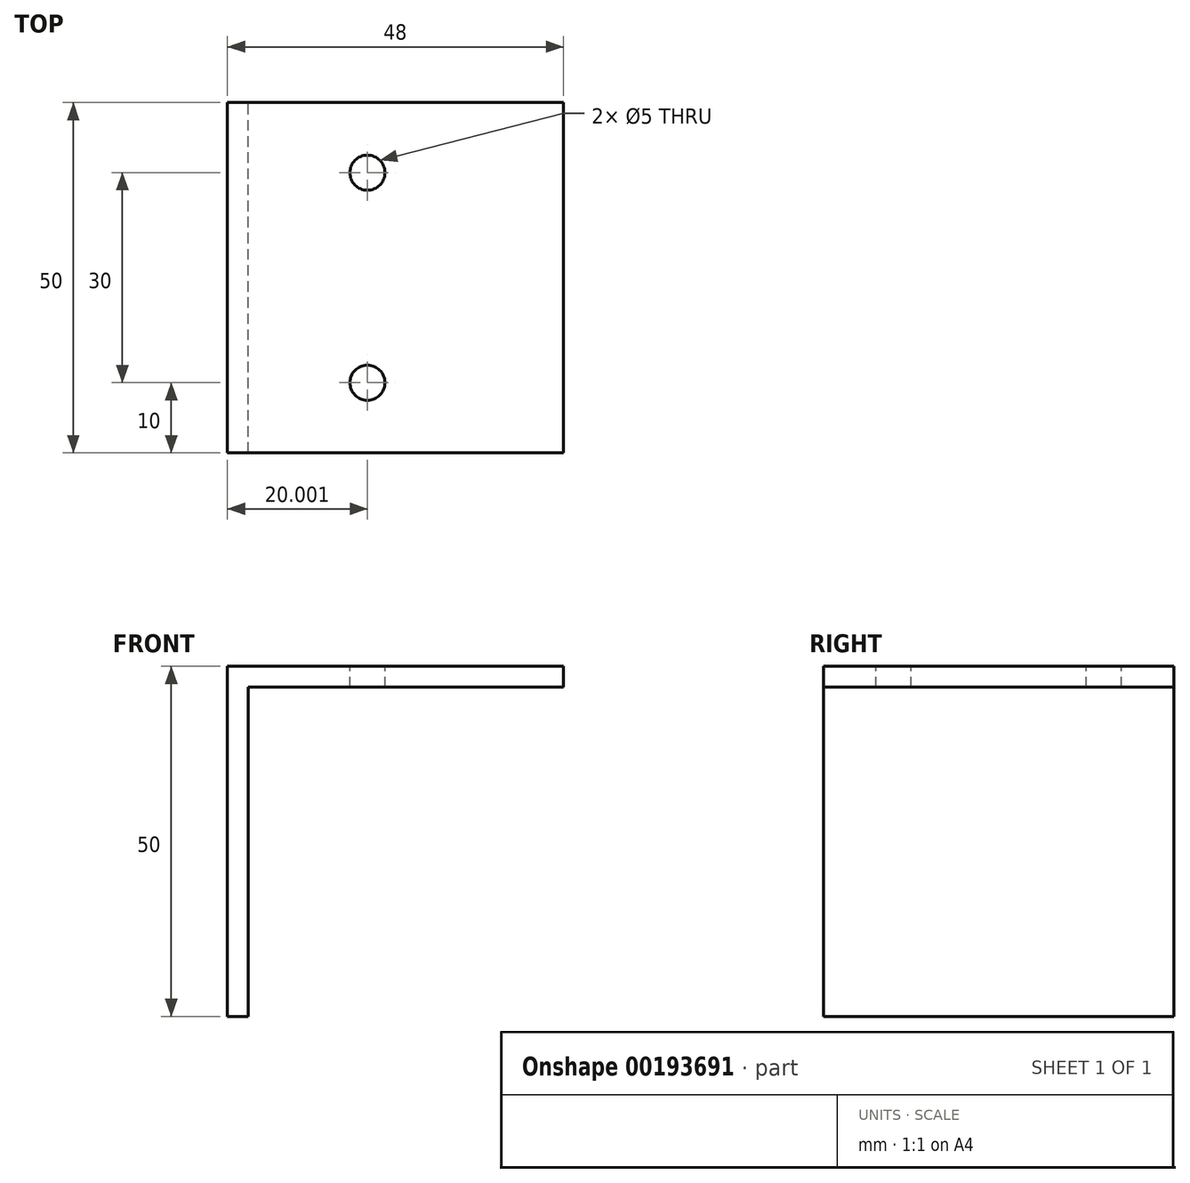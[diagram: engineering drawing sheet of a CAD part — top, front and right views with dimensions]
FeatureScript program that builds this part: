
annotation { "Feature Type Name" : "Feature", "Feature Type Description" : "" }
export const myFeature = defineFeature(function(context is Context, id is Id, definition is map)
    precondition{}
    {
        {
            var Q0;
            Q0=qCreatedBy(makeId("Front.planeOp"),FACE);
            var sketch = newSketch(context, id + "F0", { "sketchPlane" : qUnion([Q0])});
            skLineSegment(sketch, "E0", {"start": v(-23.92, 35.83) * mm, "end": v(-23.92, -14.17) * mm});
            skLineSegment(sketch, "E1", {"start": v(-23.92, -14.17) * mm, "end": v(-20.92, -14.17) * mm});
            skLineSegment(sketch, "E2", {"start": v(-20.92, -14.17) * mm, "end": v(-20.92, 32.83) * mm});
            skLineSegment(sketch, "E3", {"start": v(-20.92, 32.83) * mm, "end": v(24.08, 32.83) * mm});
            skLineSegment(sketch, "E4", {"start": v(24.08, 32.83) * mm, "end": v(24.08, 35.83) * mm});
            skLineSegment(sketch, "E5", {"start": v(24.08, 35.83) * mm, "end": v(-23.92, 35.83) * mm});
            skSolve(sketch);
        }
        {
            var Q0;
            Q0=makeQuery(id+"F0.imprint","IMPRINT",FACE,{"disambiguationData":[TD([[makeQuery(id+"F0.imprint","IMPRINT",EDGE,{"derivedFrom":sQuery(id+"F0.wireOp",EDGE,"E0")}),1.0]])]});
            extrude(context, id + "F1", {"entities" : qUnion([Q0]), "depth" : 50 * mm});
        }
        {
            var Q0;
            Q0=makeQuery(id+"F1.opExtrude","SWEPT_FACE",FACE,{"disambiguationData":[OSD([sQuery(id+"F0.wireOp",EDGE,"E5")])]});
            var sketch = newSketch(context, id + "F2", { "sketchPlane" : qUnion([Q0])});
            skCircle(sketch, "E6", {"center": v(-3.92, -10) * mm, "radius": 2.5 * mm});
            skCircle(sketch, "E7", {"center": v(-3.92, -40) * mm, "radius": 2.5 * mm});
            skSolve(sketch);
        }
        {
            var Q0;
            Q0=makeQuery(id+"F2.imprint","IMPRINT",FACE,{"disambiguationData":[TD([[makeQuery(id+"F2.imprint","IMPRINT",EDGE,{"derivedFrom":sQuery(id+"F2.wireOp",EDGE,"E6")}),1.0]])]});
            var Q1;
            Q1=makeQuery(id+"F2.imprint","IMPRINT",FACE,{"disambiguationData":[TD([[makeQuery(id+"F2.imprint","IMPRINT",EDGE,{"derivedFrom":sQuery(id+"F2.wireOp",EDGE,"E7")}),1.0]])]});
            extrude(context, id + "F3", {"entities" : qUnion([Q0, Q1]), "operationType" : NewBodyOperationType.REMOVE, "oppositeDirection" : true, "depth" : 25 * mm});
        }
    });
